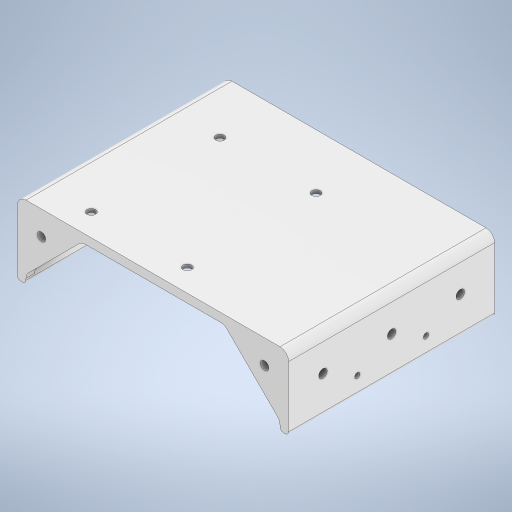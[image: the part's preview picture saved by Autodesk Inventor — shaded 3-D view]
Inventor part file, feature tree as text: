
AUTODESK INVENTOR PART (.ipt)
format: ipt  version: 2024.3 (Build 283343000, 343)  size: 423,936 bytes
history: native  units: mm
features: sketch x9, extrude x7, fillet x3, hole x2, other x1, projected_geometry x1
ambient origin geometry x8: Origin, YZ Plane, XZ Plane, XY Plane, X Axis, Y Axis, Z Axis, Center Point
bodies: Body1 (feature_tree)
feature tree (23):
  other  "ソリッド1"
  extrude  "押し出し1"  Depth=158.0mm
  extrude  "押し出し3"  Depth=250.0mm
  extrude  "押し出し4"  Depth=5.0mm
  hole  "穴2"  [1 undecoded]
  extrude  "押し出し5"  Depth=50.0mm
  extrude  "押し出し6"  Depth=50.0mm
  fillet  "フィレット4"  Radius=30.0mm
  fillet  "フィレット6"  Radius=5.0mm
  extrude  "押し出し8"  Depth=50.0mm
  fillet  "フィレット7"  Radius=50.0mm
  extrude  "押し出し9"  Depth=30.0mm
  hole  "穴3"  [1 undecoded]
  sketch  "スケッチ1"
  sketch  "スケッチ5"
  sketch  "スケッチ6"
  sketch  "スケッチ7"
  sketch  "スケッチ8"
  sketch  "スケッチ9"
  sketch  "スケッチ12"
  projected_geometry  "投影ループ1"
  sketch  "スケッチ13"
  sketch  "スケッチ14"
note: 2 required parameter values undecoded (feature->parameter linkage not recoverable at this tier; creation-order binding heuristic only, values carry confidence <= 0.55)
